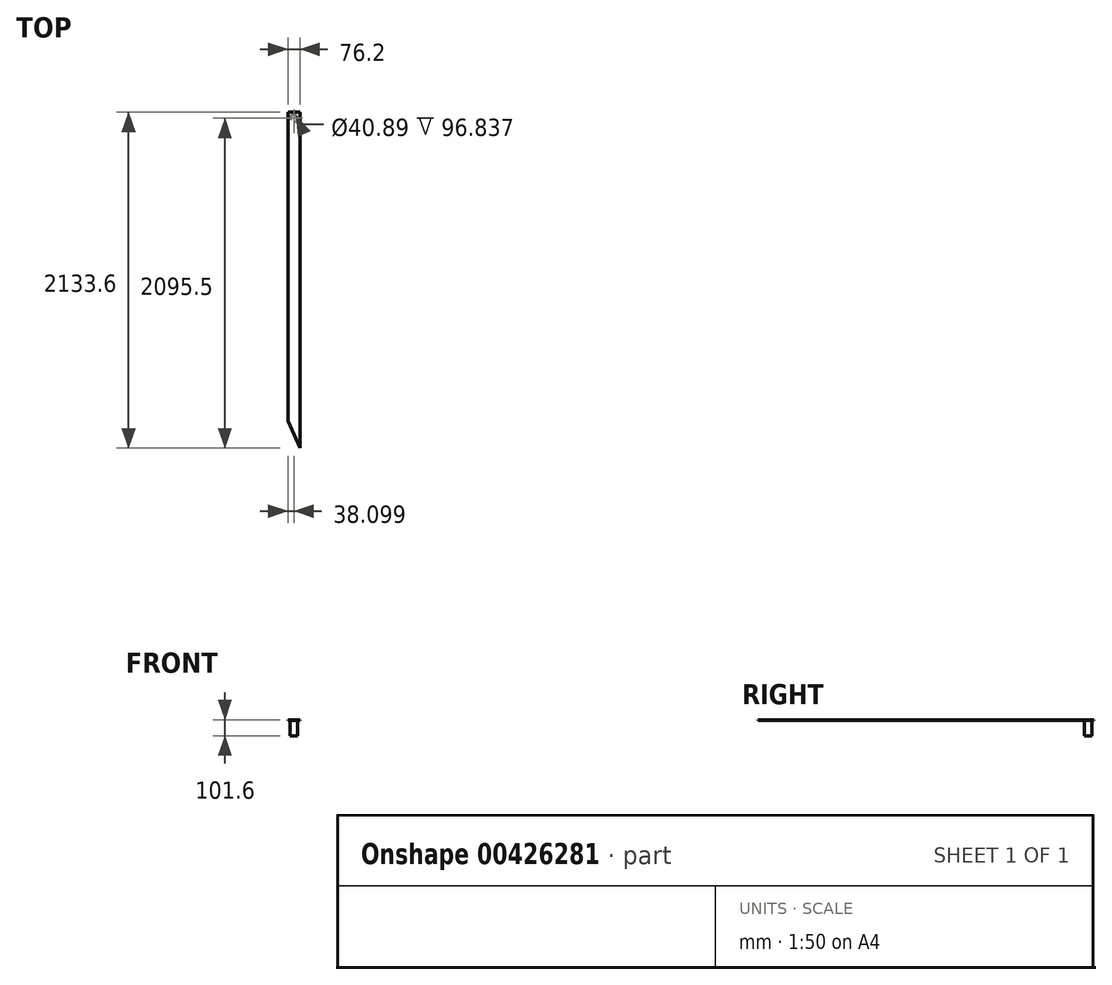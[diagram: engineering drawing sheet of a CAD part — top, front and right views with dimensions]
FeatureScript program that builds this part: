
annotation { "Feature Type Name" : "Feature", "Feature Type Description" : "" }
export const myFeature = defineFeature(function(context is Context, id is Id, definition is map)
    precondition{}
    {
        {
            var Q0;
            Q0=qCreatedBy(makeId("Top.planeOp"),FACE);
            var sketch = newSketch(context, id + "F0", { "sketchPlane" : qUnion([Q0])});
            skLineSegment(sketch, "E0.bottom", {"start": v(337.86, 853.8) * mm, "end": v(414.06, 853.8) * mm});
            skLineSegment(sketch, "E0.top", {"start": v(337.86, -1279.8) * mm, "end": v(414.06, -1279.8) * mm});
            skLineSegment(sketch, "E0.left", {"start": v(337.86, 853.8) * mm, "end": v(337.86, -1279.8) * mm});
            skLineSegment(sketch, "E0.right", {"start": v(414.06, 853.8) * mm, "end": v(414.06, -1279.8) * mm});
            skSolve(sketch);
        }
        {
            var Q0;
            Q0=qSketchRegion(id+"F0",true);
            extrude(context, id + "F1", {"entities" : qUnion([Q0]), "oppositeDirection" : true, "depth" : 4.76 * mm});
        }
        {
            var Q0;
            Q0=makeQuery(id+"F1.opExtrude","CAP_FACE",FACE,{"disambiguationData":[OSD([sQuery(id+"F0.wireOp",EDGE,"E0.bottom"),sQuery(id+"F0.wireOp",EDGE,"E0.top"),sQuery(id+"F0.wireOp",EDGE,"E0.left"),sQuery(id+"F0.wireOp",EDGE,"E0.right")])],"isStart":true});
            var sketch = newSketch(context, id + "F2", { "sketchPlane" : qUnion([Q0])});
            skCircle(sketch, "E1", {"center": v(375.96, 815.7) * mm, "radius": 24.13 * mm});
            skCircle(sketch, "E2", {"center": v(375.96, 815.7) * mm, "radius": 20.45 * mm});
            skSolve(sketch);
        }
        {
            var Q0;
            Q0=makeQuery(id+"F2.imprint","IMPRINT",FACE,{"disambiguationData":[TD([[makeQuery(id+"F2.imprint","IMPRINT",EDGE,{"derivedFrom":sQuery(id+"F2.wireOp",EDGE,"E1")}),1.0]])]});
            var Q1;
            Q1=sQuery(id+"F2.wireOp",EDGE,"E1");
            var Q2;
            Q2=sQuery(id+"F2.wireOp",EDGE,"E2");
            extrude(context, id + "F3", {"entities" : qUnion([Q0]), "operationType" : NewBodyOperationType.ADD, "surfaceEntities" : qUnion([Q1, Q2]), "oppositeDirection" : true, "depth" : 101.6 * mm});
        }
        {
            var Q0;
            {var subQ0=sQuery(id+"F0.wireOp",EDGE,"E0.left");var subQ1=sQuery(id+"F0.wireOp",EDGE,"E0.top");var subQ2=sQuery(id+"F0.wireOp",EDGE,"E0.right");var subQ3=sQuery(id+"F0.wireOp",EDGE,"E0.bottom");Q0=makeQuery(id+"F3.boolean.opBoolean","SPLIT",FACE,{"disambiguationData":[TD([makeQuery(id+"F1.opExtrude","SWEPT_FACE",FACE,{"disambiguationData":[OSD([subQ3])]})])],"derivedFrom":makeQuery(id+"F1.opExtrude","CAP_FACE",FACE,{"disambiguationData":[OSD([subQ3,subQ1,subQ0,subQ2])],"isStart":false})});}
            var sketch = newSketch(context, id + "F4", { "sketchPlane" : qUnion([Q0])});
            skLineSegment(sketch, "E3", {"start": v(414.06, 1279.8) * mm, "end": v(337.86, 1107.85) * mm});
            skLineSegment(sketch, "E4", {"start": v(337.86, 1107.85) * mm, "end": v(337.86, 1279.8) * mm});
            skLineSegment(sketch, "E5", {"start": v(337.86, 1279.8) * mm, "end": v(414.06, 1279.8) * mm});
            skSolve(sketch);
        }
        {
            var Q0;
            Q0=makeQuery(id+"F4.imprint","IMPRINT",FACE,{"disambiguationData":[TD([[makeQuery(id+"F4.imprint","IMPRINT",EDGE,{"derivedFrom":sQuery(id+"F4.wireOp",EDGE,"E3")}),-1.0]])]});
            extrude(context, id + "F5", {"entities" : qUnion([Q0]), "operationType" : NewBodyOperationType.REMOVE, "oppositeDirection" : true, "depth" : 35.81 * mm});
        }
    });
